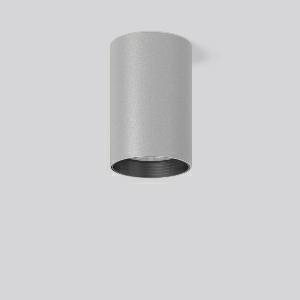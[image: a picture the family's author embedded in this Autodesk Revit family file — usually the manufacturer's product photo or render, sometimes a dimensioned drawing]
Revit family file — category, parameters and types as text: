
# Revit family: heledon_maxi_a_931221_004_1_842a
name_source: partatom
category: Lighting Fixtures
units: mm (PartAtom-declared; Revit-internal decimal feet)

## family parameters
Cut with Voids When Loaded = No
Host = Face
Light Source = No
Part Type = Normal
Room Calculation Point = No
Round Connector Dimension = Use Diameter
Shared = No

## types (1)
- HELEDON maxi A (1 x LED Modul 940, 2850 lm, 4000)
    Apparent Load = 25 VA
    Approval mark = CE
    CIE Flux Codes = 96 100 100 100 100
    Color Rendering = 92
    Color Temperature = 4000
    Default Elevation = 1800 mm
    Description = Series: HELEDON maxi
Cylindrical surface-mounted downlight. Housing: die-cast aluminium, powder-coated. Internal ceiling frame polycarbonate with bayonet mounting. Black plastic ring and recessed LED to prevent glare from the side. Optical assembly with lens made of plastic (polycarbonate) for the best homogeneous light distribution - can be changed without tools. Best colour rendering index Ra>90. Suitable for Ceiling mounting. Easy installation with a separate ceiling frame with bayonet mounting and plug connection. Driver integrated. Connected via plug-in connector. High quality converter without flickering and stroboscopic effect. The following accessories can be mounted without use of tools: interchangeable lenses, decorative glasses, honeycomb louvre, clear and frosted diffusers, white interchangeable plastic ring. 
Colour: silver
Diameter: 123 mm
Height: 183 mm
Lamp: LED
Socket: without socket
Colour temperature: 4000K
Colour rendering index (CRI): 92
System power: 25 W
Rated luminous flux: 2850 lm
Luminous efficiency: 114 lm/W
Control gear: Regulated power supply
Protection class: I
Type of protection: IP 20
    Height = 183 mm
    Lamp = 1 x LED Modul 940
    Lamp Light Flux = 2850 lm
    Lamp count = 1
    Length = 123 mm
    Lifetime = 50000 h
    Luminous efficacy = 114 lm/W
    Manufacturer = RZB
    ModVariant = No
    Model = 931221.004.1
    Mounting Place = Ceiling
    Mounting Type = Surface mounted
    Number of Poles = 1
    OnlyDefault = Yes
    Power Factor = 1
    Product Name = HELEDON maxi A
    Product group = Surface mounted downlights
    ProductGroupID = 302
    Protection Class = Protection class I
    Protection Degree = IP 20
    RLX_Detail_Level = 1
    RLX_Emergency_Light_Flux = 0 lm
    RLX_Emergency_Type = 0
    RLX_Emergency_Type_DB = No
    RlxData = <blob elided: 100801 chars, md5=37d9b938>
    Socket = socket
    Standby Power = 0 W
    System Light Flux = 2850 lm
    System Power = 25 W
    Type Comments = Product without accessories
    Type Image = 931193.004.jpg
    URL = http://relux.com
    VarID = ---
    Voltage = 230 V
    Voltage Range = 220-240 V
    Weight = 0.00 kg
    Width = 0 mm  [stored 0 ft]

note: [stored X ft] marks values corroborated as IEEE doubles in the binary element streams (Revit-internal decimal feet)

## geometry (parser evidence)
native form markers: Blend x4, Sweep x10
no freeform markers — native parametric forms only
